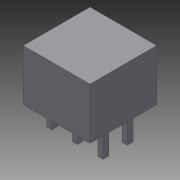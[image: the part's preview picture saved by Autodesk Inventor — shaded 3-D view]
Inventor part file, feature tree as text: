
AUTODESK INVENTOR PART (.ipt)
format: ipt  version: 2015 (Build 190159000, 159)  size: 138,752 bytes
history: native  units: mm
features: extrude x2, sketch x2, other x1
ambient origin geometry x8: Origin, YZ Plane, XZ Plane, XY Plane, X Axis, Y Axis, Z Axis, Center Point
bodies: Body1 (feature_tree)
feature tree (5):
  other  "ソリッド1"
  extrude  "押し出し1"  Depth=0.98mm
  extrude  "押し出し2"  Depth=1.15mm
  sketch  "スケッチ1"
  sketch  "スケッチ2"
